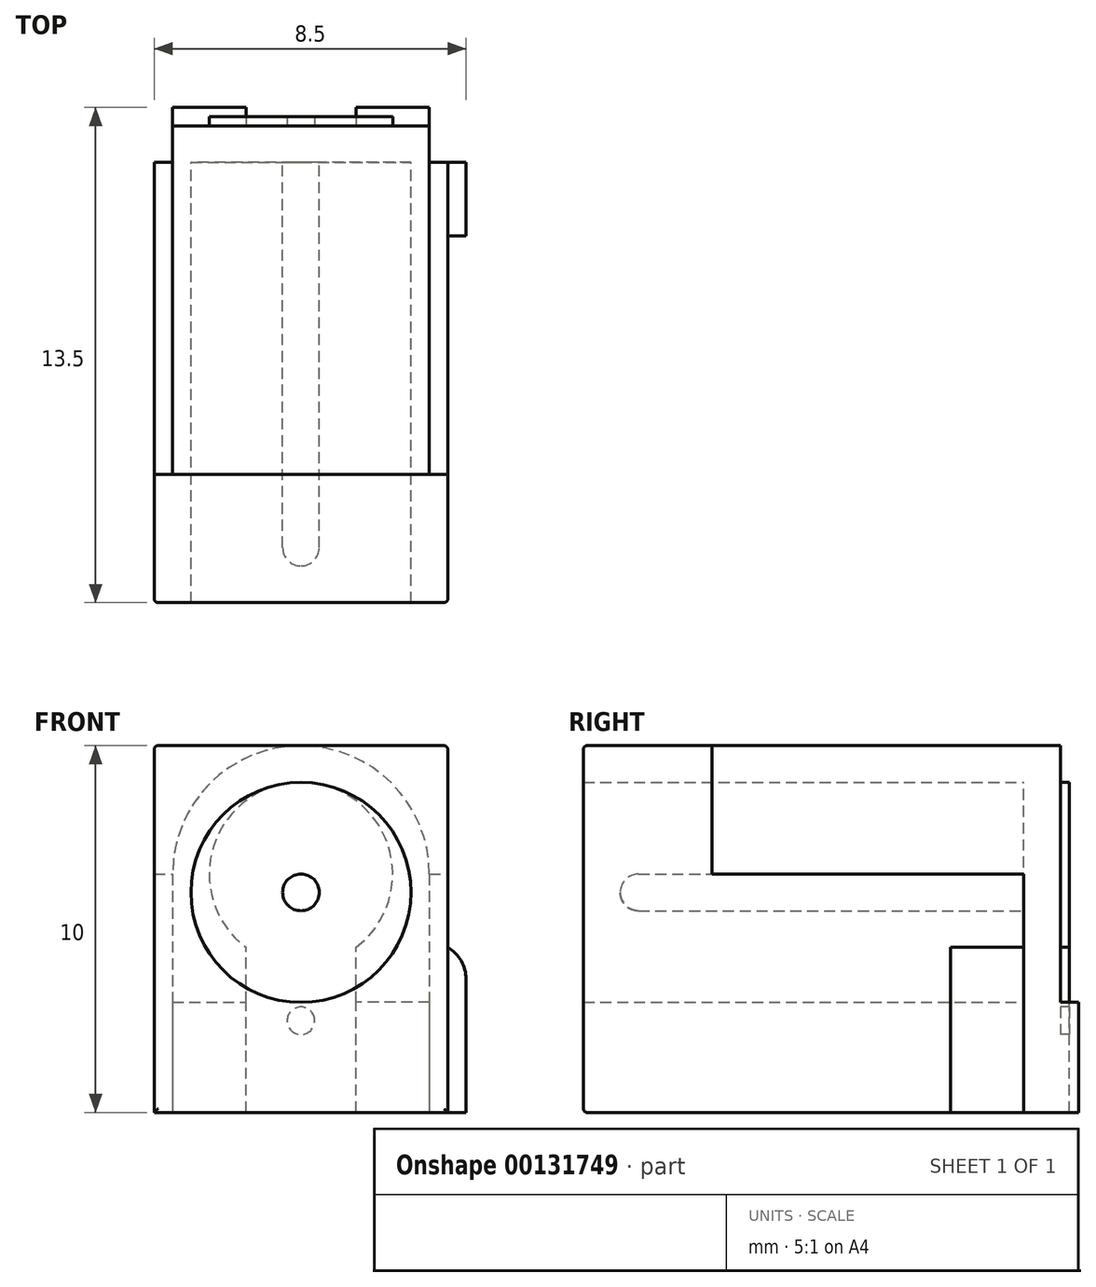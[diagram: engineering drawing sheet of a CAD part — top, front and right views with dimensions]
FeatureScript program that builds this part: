
annotation { "Feature Type Name" : "Feature", "Feature Type Description" : "" }
export const myFeature = defineFeature(function(context is Context, id is Id, definition is map)
    precondition{}
    {
        {
            var Q0;
            Q0=qCreatedBy(makeId("Front.planeOp"),FACE);
            var sketch = newSketch(context, id + "F0", { "sketchPlane" : qUnion([Q0])});
            skLineSegment(sketch, "E0.bottom", {"start": v(-33.98, 12.36) * mm, "end": v(-25.98, 12.36) * mm});
            skLineSegment(sketch, "E0.top", {"start": v(-33.98, 2.36) * mm, "end": v(-25.98, 2.36) * mm});
            skLineSegment(sketch, "E0.left", {"start": v(-33.98, 12.36) * mm, "end": v(-33.98, 2.36) * mm});
            skLineSegment(sketch, "E0.right", {"start": v(-25.98, 12.36) * mm, "end": v(-25.98, 2.36) * mm});
            skCircle(sketch, "E1", {"center": v(-29.98, 8.36) * mm, "radius": 3 * mm});
            skPoint(sketch, "E1.centerSnap0", {"position": v(-29.98, 12.36) * mm});
            skSolve(sketch);
        }
        {
            var Q0;
            Q0=makeQuery(id+"F0.imprint","IMPRINT",FACE,{"disambiguationData":[TD([[makeQuery(id+"F0.imprint","IMPRINT",EDGE,{"derivedFrom":sQuery(id+"F0.wireOp",EDGE,"E0.bottom")}),-1.0]])]});
            extrude(context, id + "F1", {"entities" : qUnion([Q0]), "depth" : 12 * mm});
        }
        {
            var Q0;
            Q0=makeQuery(id+"F1.opExtrude","SWEPT_FACE",FACE,{"disambiguationData":[OSD([sQuery(id+"F0.wireOp",EDGE,"E0.left")])]});
            var sketch = newSketch(context, id + "F2", { "sketchPlane" : qUnion([Q0])});
            skLineSegment(sketch, "E2.bottom", {"start": v(0, 12.36) * mm, "end": v(-1, 12.36) * mm});
            skLineSegment(sketch, "E2.top", {"start": v(0, 2.36) * mm, "end": v(-1, 2.36) * mm});
            skLineSegment(sketch, "E2.left", {"start": v(0, 12.36) * mm, "end": v(0, 2.36) * mm});
            skLineSegment(sketch, "E2.right", {"start": v(-1, 12.36) * mm, "end": v(-1, 2.36) * mm});
            skSolve(sketch);
        }
        {
            var Q0;
            Q0=qSketchRegion(id+"F2",true);
            var Q1;
            Q1=makeQuery(id+"F1.opExtrude","SWEPT_FACE",FACE,{"disambiguationData":[OSD([sQuery(id+"F0.wireOp",EDGE,"E0.right")])]});
            extrude(context, id + "F3", {"entities" : qUnion([Q0]), "operationType" : NewBodyOperationType.ADD, "endBound" : BoundingType.UP_TO_SURFACE, "oppositeDirection" : true, "endBoundEntityFace" : qUnion([Q1]), "depth" : 25 * mm});
        }
        {
            var Q0;
            Q0=makeQuery(id+"F3.opExtrude","SWEPT_FACE",FACE,{"disambiguationData":[OSD([sQuery(id+"F2.wireOp",EDGE,"E2.right")])]});
            var sketch = newSketch(context, id + "F4", { "sketchPlane" : qUnion([Q0])});
            skLineSegment(sketch, "E3", {"start": v(25.98, 12.36) * mm, "end": v(33.98, 12.36) * mm});
            skLineSegment(sketch, "E4", {"start": v(29.98, 12.36) * mm, "end": v(29.98, 8.86) * mm});
            skCircle(sketch, "E5", {"center": v(29.98, 8.86) * mm, "radius": 3.5 * mm});
            skLineSegment(sketch, "E6", {"start": v(33.98, 8.86) * mm, "end": v(25.98, 8.86) * mm});
            skLineSegment(sketch, "E7", {"start": v(26.48, 8.86) * mm, "end": v(26.48, 2.36) * mm});
            skLineSegment(sketch, "E8", {"start": v(33.48, 8.86) * mm, "end": v(33.48, 2.36) * mm});
            skSolve(sketch);
        }
        {
            var Q0;
            {var subQ0=sQuery(id+"F4.wireOp",EDGE,"E3");var subQ1=makeQuery(id+"F3.opExtrude","CAP_EDGE",EDGE,{"disambiguationData":[OSD([sQuery(id+"F2.wireOp",EDGE,"E2.right")])],"isStart":true});var subQ2=makeQuery(id+"F4.imprint","INTERSECT",VERTEX,{"derivedFrom":[subQ1,subQ0]});Q0=makeQuery(id+"F4.imprint","IMPRINT",FACE,{"disambiguationData":[TD([[makeQuery(id+"F4.imprint","IMPRINT",EDGE,{"disambiguationData":[TD([[subQ2,-1.0]])],"derivedFrom":subQ1}),-1.0]])]});}
            var Q1;
            {var subQ0=sQuery(id+"F4.wireOp",EDGE,"E3");var subQ1=makeQuery(id+"F3.opExtrude","TWEAK_EDGE",EDGE,{"derivedFrom":[makeQuery(id+"F1.opExtrude","SWEPT_FACE",FACE,{"disambiguationData":[OSD([sQuery(id+"F0.wireOp",EDGE,"E0.right")])]}),makeQuery(id+"F2.imprint","IMPRINT",EDGE,{"derivedFrom":sQuery(id+"F2.wireOp",EDGE,"E2.right")})]});var subQ2=makeQuery(id+"F4.imprint","INTERSECT",VERTEX,{"derivedFrom":[subQ1,subQ0]});Q1=makeQuery(id+"F4.imprint","IMPRINT",FACE,{"disambiguationData":[TD([[makeQuery(id+"F4.imprint","IMPRINT",EDGE,{"disambiguationData":[TD([[subQ2,-1.0]])],"derivedFrom":subQ0}),-1.0]])]});}
            extrude(context, id + "F5", {"entities" : qUnion([Q0, Q1]), "operationType" : NewBodyOperationType.REMOVE, "oppositeDirection" : true, "depth" : 9.5 * mm});
        }
        {
            var Q0;
            {var subQ4=sQuery(id+"F4.wireOp",EDGE,"E7");Q0=makeQuery(id+"F4.imprint","IMPRINT",FACE,{"disambiguationData":[TD([[makeQuery(id+"F4.imprint","IMPRINT",EDGE,{"derivedFrom":subQ4}),-1.0]])]});}
            var Q1;
            {var subQ4=sQuery(id+"F4.wireOp",EDGE,"E8");Q1=makeQuery(id+"F4.imprint","IMPRINT",FACE,{"disambiguationData":[TD([[makeQuery(id+"F4.imprint","IMPRINT",EDGE,{"derivedFrom":subQ4}),1.0]])]});}
            extrude(context, id + "F6", {"entities" : qUnion([Q0, Q1]), "operationType" : NewBodyOperationType.REMOVE, "oppositeDirection" : true, "depth" : 1 * mm});
        }
        {
            var Q0;
            Q0=makeQuery(id+"F3.opExtrude","SWEPT_FACE",FACE,{"disambiguationData":[OSD([sQuery(id+"F2.wireOp",EDGE,"E2.left")])]});
            var sketch = newSketch(context, id + "F7", { "sketchPlane" : qUnion([Q0])});
            skCircle(sketch, "E9", {"center": v(-29.98, 8.36) * mm, "radius": 0.5 * mm});
            skSolve(sketch);
        }
        {
            var Q0;
            Q0=qSketchRegion(id+"F7",true);
            extrude(context, id + "F8", {"entities" : qUnion([Q0]), "operationType" : NewBodyOperationType.ADD, "depth" : 11 * mm});
        }
        {
            var Q0;
            Q0=makeQuery(id+"F8.opExtrude","CAP_EDGE",EDGE,{"disambiguationData":[OSD([sQuery(id+"F7.wireOp",EDGE,"E9")])],"isStart":false});
            fillet(context, id + "F9", {"entities" : qUnion([Q0]), "radius" : 0.5 * mm, "tangentPropagation" : true, "allowEdgeOverflow" : false});
        }
        {
            var Q0;
            Q0=makeQuery(id+"F1.opExtrude","CAP_EDGE",EDGE,{"disambiguationData":[OSD([sQuery(id+"F0.wireOp",EDGE,"E0.bottom")])],"isStart":false});
            var Q1;
            Q1=makeQuery(id+"F1.opExtrude","CAP_EDGE",EDGE,{"disambiguationData":[OSD([sQuery(id+"F0.wireOp",EDGE,"E0.right")])],"isStart":false});
            var Q2;
            Q2=makeQuery(id+"F1.opExtrude","CAP_EDGE",EDGE,{"disambiguationData":[OSD([sQuery(id+"F0.wireOp",EDGE,"E0.left")])],"isStart":false});
            var Q3;
            Q3=makeQuery(id+"F1.opExtrude","CAP_EDGE",EDGE,{"disambiguationData":[OSD([sQuery(id+"F0.wireOp",EDGE,"E0.top")])],"isStart":false});
            var Q4;
            {var subQ0=sQuery(id+"F0.wireOp",EDGE,"E0.right");Q4=makeQuery(id+"F3.boolean.opBoolean","MERGE",EDGE,{"derivedFrom":[makeQuery(id+"F1.opExtrude","SWEPT_EDGE",EDGE,{"disambiguationData":[OSD([sQuery(id+"F0.wireOp",EDGE,"E0.bottom"),subQ0])]}),makeQuery(id+"F3.opExtrude","TWEAK_EDGE",EDGE,{"derivedFrom":[makeQuery(id+"F1.opExtrude","SWEPT_FACE",FACE,{"disambiguationData":[OSD([subQ0])]}),makeQuery(id+"F2.imprint","IMPRINT",EDGE,{"derivedFrom":sQuery(id+"F2.wireOp",EDGE,"E2.bottom")})]})]});}
            var Q5;
            Q5=makeQuery(id+"F3.boolean.opBoolean","MERGE",EDGE,{"derivedFrom":[makeQuery(id+"F1.opExtrude","SWEPT_EDGE",EDGE,{"disambiguationData":[OSD([sQuery(id+"F0.wireOp",EDGE,"E0.bottom"),sQuery(id+"F0.wireOp",EDGE,"E0.left")])]}),makeQuery(id+"F3.opExtrude","CAP_EDGE",EDGE,{"disambiguationData":[OSD([sQuery(id+"F2.wireOp",EDGE,"E2.bottom")])],"isStart":true})]});
            fillet(context, id + "F10", {"entities" : qUnion([Q0, Q1, Q2, Q3, Q4, Q5]), "radius" : 0.1 * mm, "tangentPropagation" : true, "allowEdgeOverflow" : false});
        }
        {
            var Q0;
            Q0=makeQuery(id+"F3.opExtrude","SWEPT_FACE",FACE,{"disambiguationData":[OSD([sQuery(id+"F2.wireOp",EDGE,"E2.right")])]});
            var sketch = newSketch(context, id + "F11", { "sketchPlane" : qUnion([Q0])});
            skLineSegment(sketch, "E10.bottom", {"start": v(26.48, 2.36) * mm, "end": v(28.48, 2.36) * mm});
            skLineSegment(sketch, "E10.top", {"start": v(26.48, 5.36) * mm, "end": v(28.48, 5.36) * mm});
            skLineSegment(sketch, "E10.left", {"start": v(26.48, 2.36) * mm, "end": v(26.48, 5.36) * mm});
            skLineSegment(sketch, "E10.right", {"start": v(28.48, 2.36) * mm, "end": v(28.48, 5.36) * mm});
            skLineSegment(sketch, "E11.bottom", {"start": v(33.48, 2.36) * mm, "end": v(31.48, 2.36) * mm});
            skLineSegment(sketch, "E11.top", {"start": v(33.48, 5.36) * mm, "end": v(31.48, 5.36) * mm});
            skLineSegment(sketch, "E11.left", {"start": v(33.48, 2.36) * mm, "end": v(33.48, 5.36) * mm});
            skLineSegment(sketch, "E11.right", {"start": v(31.48, 2.36) * mm, "end": v(31.48, 5.36) * mm});
            skSolve(sketch);
        }
        {
            var Q0;
            Q0=qSketchRegion(id+"F11",true);
            extrude(context, id + "F12", {"entities" : qUnion([Q0]), "operationType" : NewBodyOperationType.ADD, "depth" : 0.5 * mm});
        }
        {
            var Q0;
            Q0=makeQuery(id+"F3.opExtrude","SWEPT_FACE",FACE,{"disambiguationData":[OSD([sQuery(id+"F2.wireOp",EDGE,"E2.right")])]});
            var sketch = newSketch(context, id + "F13", { "sketchPlane" : qUnion([Q0])});
            skCircle(sketch, "E12", {"center": v(29.98, 8.86) * mm, "radius": 2.5 * mm});
            skLineSegment(sketch, "E13", {"start": v(28.48, 2.36) * mm, "end": v(28.48, 6.86) * mm});
            skLineSegment(sketch, "E14", {"start": v(28.48, 6.86) * mm, "end": v(31.48, 6.86) * mm});
            skLineSegment(sketch, "E15", {"start": v(31.48, 6.86) * mm, "end": v(31.48, 2.36) * mm});
            skCircle(sketch, "E16", {"center": v(29.98, 4.86) * mm, "radius": 0.38 * mm});
            skSolve(sketch);
        }
        {
            var Q0;
            {var subQ0=sQuery(id+"F13.wireOp",EDGE,"E14");Q0=makeQuery(id+"F13.imprint","IMPRINT",FACE,{"disambiguationData":[TD([[makeQuery(id+"F13.imprint","IMPRINT",EDGE,{"derivedFrom":subQ0}),-1.0]])]});}
            var Q1;
            {var subQ0=sQuery(id+"F13.wireOp",EDGE,"E14");Q1=makeQuery(id+"F13.imprint","IMPRINT",FACE,{"disambiguationData":[TD([[makeQuery(id+"F13.imprint","IMPRINT",EDGE,{"derivedFrom":subQ0}),1.0]])]});}
            var Q2;
            Q2=makeQuery(id+"F13.imprint","IMPRINT",FACE,{"disambiguationData":[TD([[makeQuery(id+"F13.imprint","IMPRINT",EDGE,{"derivedFrom":sQuery(id+"F13.wireOp",EDGE,"E16")}),-1.0]])]});
            extrude(context, id + "F14", {"entities" : qUnion([Q0, Q1, Q2]), "operationType" : NewBodyOperationType.ADD, "depth" : 0.25 * mm});
        }
        {
            var Q0;
            {var subQ0=sQuery(id+"F0.wireOp",EDGE,"E0.right");Q0=makeQuery(id+"F3.boolean.opBoolean","MERGE",FACE,{"derivedFrom":[makeQuery(id+"F1.opExtrude","SWEPT_FACE",FACE,{"disambiguationData":[OSD([subQ0])]}),makeQuery(id+"F3.opExtrude","CAP_FACE",FACE,{"disambiguationData":[OSD([subQ0])],"isStart":false})]});}
            var sketch = newSketch(context, id + "F15", { "sketchPlane" : qUnion([Q0])});
            skLineSegment(sketch, "E17.bottom", {"start": v(0, 2.36) * mm, "end": v(-2, 2.36) * mm});
            skLineSegment(sketch, "E17.top", {"start": v(0, 6.86) * mm, "end": v(-2, 6.86) * mm});
            skLineSegment(sketch, "E17.left", {"start": v(0, 2.36) * mm, "end": v(0, 6.86) * mm});
            skLineSegment(sketch, "E17.right", {"start": v(-2, 2.36) * mm, "end": v(-2, 6.86) * mm});
            skSolve(sketch);
        }
        {
            var Q0;
            Q0=qSketchRegion(id+"F15",true);
            extrude(context, id + "F16", {"entities" : qUnion([Q0]), "operationType" : NewBodyOperationType.ADD, "depth" : 0.5 * mm});
        }
        {
            var Q0;
            Q0=makeQuery(id+"F16.opExtrude","CAP_EDGE",EDGE,{"disambiguationData":[OSD([sQuery(id+"F15.wireOp",EDGE,"E17.top")])],"isStart":false});
            fillet(context, id + "F17", {"entities" : qUnion([Q0]), "radius" : 1 * mm, "allowEdgeOverflow" : false});
        }
    });
